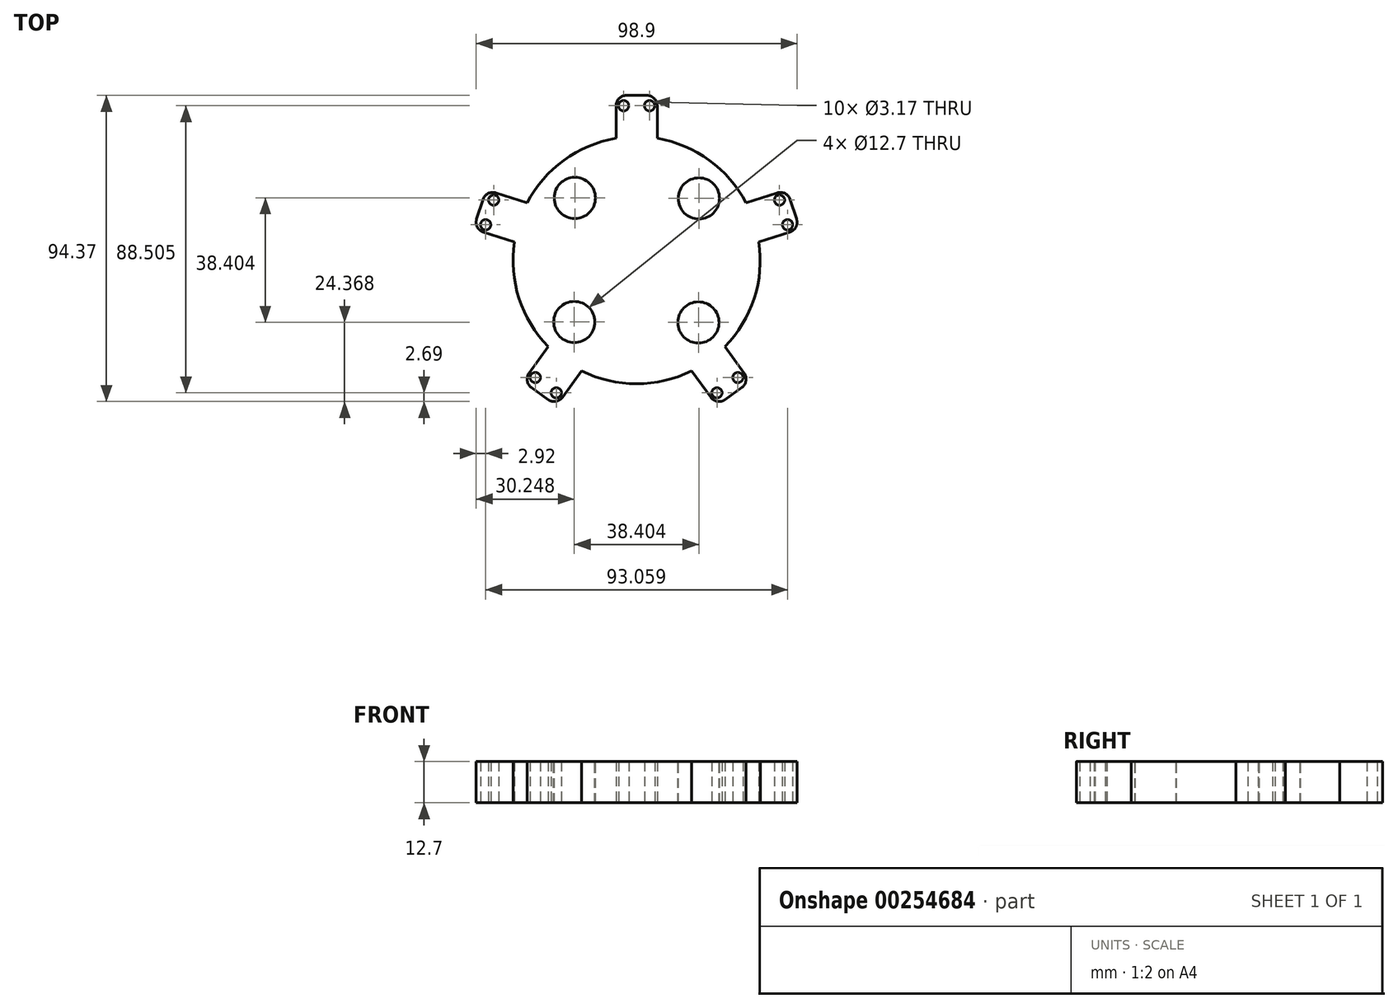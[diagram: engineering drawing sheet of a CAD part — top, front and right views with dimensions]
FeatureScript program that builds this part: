
annotation { "Feature Type Name" : "Feature", "Feature Type Description" : "" }
export const myFeature = defineFeature(function(context is Context, id is Id, definition is map)
    precondition{}
    {
        {
            var Q0;
            Q0=qCreatedBy(makeId("Top.planeOp"),FACE);
            var sketch = newSketch(context, id + "F0", { "sketchPlane" : qUnion([Q0])});
            skArc(sketch, "E0", {"start": v(-6.35, 37.57) * mm, "mid": v(-22.4, 30.82) * mm, "end": v(-33.77, 17.65) * mm});
            skLineSegment(sketch, "E1", {"start": v(0, 0) * mm, "end": v(0, 50.8) * mm, "construction": true});
            skLineSegment(sketch, "E2", {"start": v(-6.35, 37.23) * mm, "end": v(-6.35, 47.63) * mm});
            skLineSegment(sketch, "E3.MirrorCS", {"start": v(6.35, 37.23) * mm, "end": v(6.35, 47.63) * mm});
            skLineSegment(sketch, "E4", {"start": v(-3.17, 50.8) * mm, "end": v(3.17, 50.8) * mm});
            skCircle(sketch, "E5", {"center": v(-4, 47.63) * mm, "radius": 1.59 * mm});
            skCircle(sketch, "E6.MirrorC", {"center": v(4, 47.63) * mm, "radius": 1.59 * mm});
            skPoint(sketch, "E7.visualSharp", {"position": v(6.35, 50.8) * mm});
            skArc(sketch, "E7.filletArc", {"start": v(6.35, 47.63) * mm, "mid": v(5.42, 49.87) * mm, "end": v(3.17, 50.8) * mm});
            skPoint(sketch, "E8.visualSharp", {"position": v(-6.35, 50.8) * mm});
            skArc(sketch, "E8.filletArc", {"start": v(-3.17, 50.8) * mm, "mid": v(-5.42, 49.87) * mm, "end": v(-6.35, 47.63) * mm});
            skPoint(sketch, "E9.1.0", {"position": v(-50.28, 9.66) * mm});
            skLineSegment(sketch, "E9.1.1", {"start": v(-33.44, 17.54) * mm, "end": v(-43.33, 20.76) * mm});
            skLineSegment(sketch, "E9.1.2", {"start": v(0, 0) * mm, "end": v(-48.31, 15.7) * mm, "construction": true});
            skArc(sketch, "E9.1.3", {"start": v(-37.7, 5.57) * mm, "mid": v(-36.24, -11.77) * mm, "end": v(-27.22, -26.66) * mm});
            skPoint(sketch, "E9.1.4", {"position": v(-46.35, 21.74) * mm});
            skLineSegment(sketch, "E9.1.5", {"start": v(-37.37, 5.46) * mm, "end": v(-47.26, 8.68) * mm});
            skLineSegment(sketch, "E9.1.6", {"start": v(-49.3, 12.68) * mm, "end": v(-47.33, 18.72) * mm});
            skCircle(sketch, "E9.1.7", {"center": v(-46.53, 10.91) * mm, "radius": 1.59 * mm});
            skArc(sketch, "E9.1.8", {"start": v(-43.33, 20.76) * mm, "mid": v(-45.75, 20.57) * mm, "end": v(-47.33, 18.72) * mm});
            skCircle(sketch, "E9.1.9", {"center": v(-44.06, 18.52) * mm, "radius": 1.59 * mm});
            skArc(sketch, "E9.1.10", {"start": v(-49.3, 12.68) * mm, "mid": v(-49.1, 10.26) * mm, "end": v(-47.26, 8.68) * mm});
            skPoint(sketch, "E9.2.0", {"position": v(-24.72, -44.83) * mm});
            skLineSegment(sketch, "E9.2.1", {"start": v(-27.02, -26.38) * mm, "end": v(-33.13, -34.8) * mm});
            skLineSegment(sketch, "E9.2.2", {"start": v(0, 0) * mm, "end": v(-29.86, -41.1) * mm, "construction": true});
            skPoint(sketch, "E9.2.4", {"position": v(-35, -37.37) * mm});
            skLineSegment(sketch, "E9.2.5", {"start": v(-16.74, -33.85) * mm, "end": v(-22.86, -42.26) * mm});
            skLineSegment(sketch, "E9.2.6", {"start": v(-27.3, -42.96) * mm, "end": v(-32.43, -39.23) * mm});
            skCircle(sketch, "E9.2.7", {"center": v(-24.76, -40.88) * mm, "radius": 1.59 * mm});
            skArc(sketch, "E9.2.8", {"start": v(-33.13, -34.8) * mm, "mid": v(-33.7, -37.16) * mm, "end": v(-32.43, -39.23) * mm});
            skCircle(sketch, "E9.2.9", {"center": v(-31.23, -36.18) * mm, "radius": 1.59 * mm});
            skArc(sketch, "E9.2.10", {"start": v(-27.3, -42.96) * mm, "mid": v(-24.93, -43.53) * mm, "end": v(-22.86, -42.26) * mm});
            skPoint(sketch, "E9.3.0", {"position": v(35, -37.37) * mm});
            skLineSegment(sketch, "E9.3.1", {"start": v(16.74, -33.85) * mm, "end": v(22.86, -42.26) * mm});
            skLineSegment(sketch, "E9.3.2", {"start": v(0, 0) * mm, "end": v(29.86, -41.1) * mm, "construction": true});
            skArc(sketch, "E9.3.3", {"start": v(-37.7, 5.57) * mm, "mid": v(-36.24, -11.77) * mm, "end": v(-27.22, -26.66) * mm});
            skPoint(sketch, "E9.3.4", {"position": v(24.72, -44.83) * mm});
            skLineSegment(sketch, "E9.3.5", {"start": v(27.02, -26.38) * mm, "end": v(33.13, -34.8) * mm});
            skLineSegment(sketch, "E9.3.6", {"start": v(32.43, -39.23) * mm, "end": v(27.3, -42.96) * mm});
            skCircle(sketch, "E9.3.7", {"center": v(31.23, -36.18) * mm, "radius": 1.59 * mm});
            skArc(sketch, "E9.3.8", {"start": v(22.86, -42.26) * mm, "mid": v(24.93, -43.53) * mm, "end": v(27.3, -42.96) * mm});
            skCircle(sketch, "E9.3.9", {"center": v(24.76, -40.88) * mm, "radius": 1.59 * mm});
            skArc(sketch, "E9.3.10", {"start": v(32.43, -39.23) * mm, "mid": v(33.7, -37.16) * mm, "end": v(33.13, -34.8) * mm});
            skPoint(sketch, "E9.4.0", {"position": v(46.35, 21.74) * mm});
            skLineSegment(sketch, "E9.4.1", {"start": v(37.37, 5.46) * mm, "end": v(47.26, 8.68) * mm});
            skLineSegment(sketch, "E9.4.2", {"start": v(0, 0) * mm, "end": v(48.31, 15.7) * mm, "construction": true});
            skArc(sketch, "E9.4.3", {"start": v(-37.7, 5.57) * mm, "mid": v(-36.24, -11.77) * mm, "end": v(-27.22, -26.66) * mm});
            skPoint(sketch, "E9.4.4", {"position": v(50.28, 9.66) * mm});
            skLineSegment(sketch, "E9.4.5", {"start": v(33.44, 17.54) * mm, "end": v(43.33, 20.76) * mm});
            skLineSegment(sketch, "E9.4.6", {"start": v(47.33, 18.72) * mm, "end": v(49.3, 12.68) * mm});
            skCircle(sketch, "E9.4.7", {"center": v(44.06, 18.52) * mm, "radius": 1.59 * mm});
            skArc(sketch, "E9.4.8", {"start": v(47.26, 8.68) * mm, "mid": v(49.1, 10.26) * mm, "end": v(49.3, 12.68) * mm});
            skCircle(sketch, "E9.4.9", {"center": v(46.53, 10.91) * mm, "radius": 1.59 * mm});
            skArc(sketch, "E9.4.10", {"start": v(47.33, 18.72) * mm, "mid": v(45.75, 20.57) * mm, "end": v(43.33, 20.76) * mm});
            skArc(sketch, "E10.trimOffspring", {"start": v(-16.94, -34.12) * mm, "mid": v(0, -38.1) * mm, "end": v(16.94, -34.12) * mm});
            skArc(sketch, "E11.trimOffspring", {"start": v(27.22, -26.66) * mm, "mid": v(36.24, -11.77) * mm, "end": v(37.7, 5.57) * mm});
            skArc(sketch, "E12.trimOffspring", {"start": v(33.77, 17.65) * mm, "mid": v(22.4, 30.82) * mm, "end": v(6.35, 37.57) * mm});
            skSolve(sketch);
        }
        {
            var Q0;
            Q0 = qSketchRegion(id + "F0", true);
            extrude(context, id + "F1", {"entities" : qUnion([Q0]), "depth" : 12.7 * mm});
        }
        {
            var Q0;
            Q0=makeQuery(id+"F1.opExtrude","CAP_FACE",FACE,{"disambiguationData":[OSD([sQuery(id+"F0.wireOp",EDGE,"E0"),sQuery(id+"F0.wireOp",EDGE,"E2"),sQuery(id+"F0.wireOp",EDGE,"E3.MirrorCS"),sQuery(id+"F0.wireOp",EDGE,"E4"),sQuery(id+"F0.wireOp",EDGE,"E5"),sQuery(id+"F0.wireOp",EDGE,"E6.MirrorC"),sQuery(id+"F0.wireOp",EDGE,"E7.filletArc"),sQuery(id+"F0.wireOp",EDGE,"E8.filletArc"),sQuery(id+"F0.wireOp",EDGE,"E9.1.1"),sQuery(id+"F0.wireOp",EDGE,"E9.1.5"),sQuery(id+"F0.wireOp",EDGE,"E9.1.6"),sQuery(id+"F0.wireOp",EDGE,"E9.1.7"),sQuery(id+"F0.wireOp",EDGE,"E9.1.8"),sQuery(id+"F0.wireOp",EDGE,"E9.1.9"),sQuery(id+"F0.wireOp",EDGE,"E9.1.10"),sQuery(id+"F0.wireOp",EDGE,"E9.2.1"),sQuery(id+"F0.wireOp",EDGE,"E9.2.5"),sQuery(id+"F0.wireOp",EDGE,"E9.2.6"),sQuery(id+"F0.wireOp",EDGE,"E9.2.7"),sQuery(id+"F0.wireOp",EDGE,"E9.2.8"),sQuery(id+"F0.wireOp",EDGE,"E9.2.9"),sQuery(id+"F0.wireOp",EDGE,"E9.2.10"),sQuery(id+"F0.wireOp",EDGE,"E9.3.1"),sQuery(id+"F0.wireOp",EDGE,"E9.3.5"),sQuery(id+"F0.wireOp",EDGE,"E9.3.6"),sQuery(id+"F0.wireOp",EDGE,"E9.3.7"),sQuery(id+"F0.wireOp",EDGE,"E9.3.8"),sQuery(id+"F0.wireOp",EDGE,"E9.3.9"),sQuery(id+"F0.wireOp",EDGE,"E9.3.10"),sQuery(id+"F0.wireOp",EDGE,"E9.4.1"),sQuery(id+"F0.wireOp",EDGE,"E9.4.5"),sQuery(id+"F0.wireOp",EDGE,"E9.4.6"),sQuery(id+"F0.wireOp",EDGE,"E9.4.7"),sQuery(id+"F0.wireOp",EDGE,"E9.4.8"),sQuery(id+"F0.wireOp",EDGE,"E9.4.9"),sQuery(id+"F0.wireOp",EDGE,"E9.4.10"),sQuery(id+"F0.wireOp",EDGE,"E9.1.3"),sQuery(id+"F0.wireOp",EDGE,"E10.trimOffspring"),sQuery(id+"F0.wireOp",EDGE,"E11.trimOffspring"),sQuery(id+"F0.wireOp",EDGE,"E12.trimOffspring")])],"isStart":false});
            var sketch = newSketch(context, id + "F2", { "sketchPlane" : qUnion([Q0])});
            skLineSegment(sketch, "E13", {"start": v(0, 50.8) * mm, "end": v(0, -38.1) * mm, "construction": true});
            skCircle(sketch, "E14", {"center": v(-19.05, 19.2) * mm, "radius": 6.35 * mm});
            skPoint(sketch, "E14.centerSnap0", {"position": v(-38.55, 19.2) * mm});
            skCircle(sketch, "E15.1.0", {"center": v(-19.2, -19.05) * mm, "radius": 6.35 * mm});
            skCircle(sketch, "E15.2.0", {"center": v(19.05, -19.2) * mm, "radius": 6.35 * mm});
            skCircle(sketch, "E15.3.0", {"center": v(19.2, 19.05) * mm, "radius": 6.35 * mm});
            skPoint(sketch, "E15.center", {"position": v(0, 0) * mm});
            skSolve(sketch);
        }
        {
            var Q0;
            Q0 = qSketchRegion(id + "F2", true);
            extrude(context, id + "F3", {"entities" : qUnion([Q0]), "operationType" : NewBodyOperationType.REMOVE, "oppositeDirection" : true, "depth" : 254 * mm});
        }
    });
